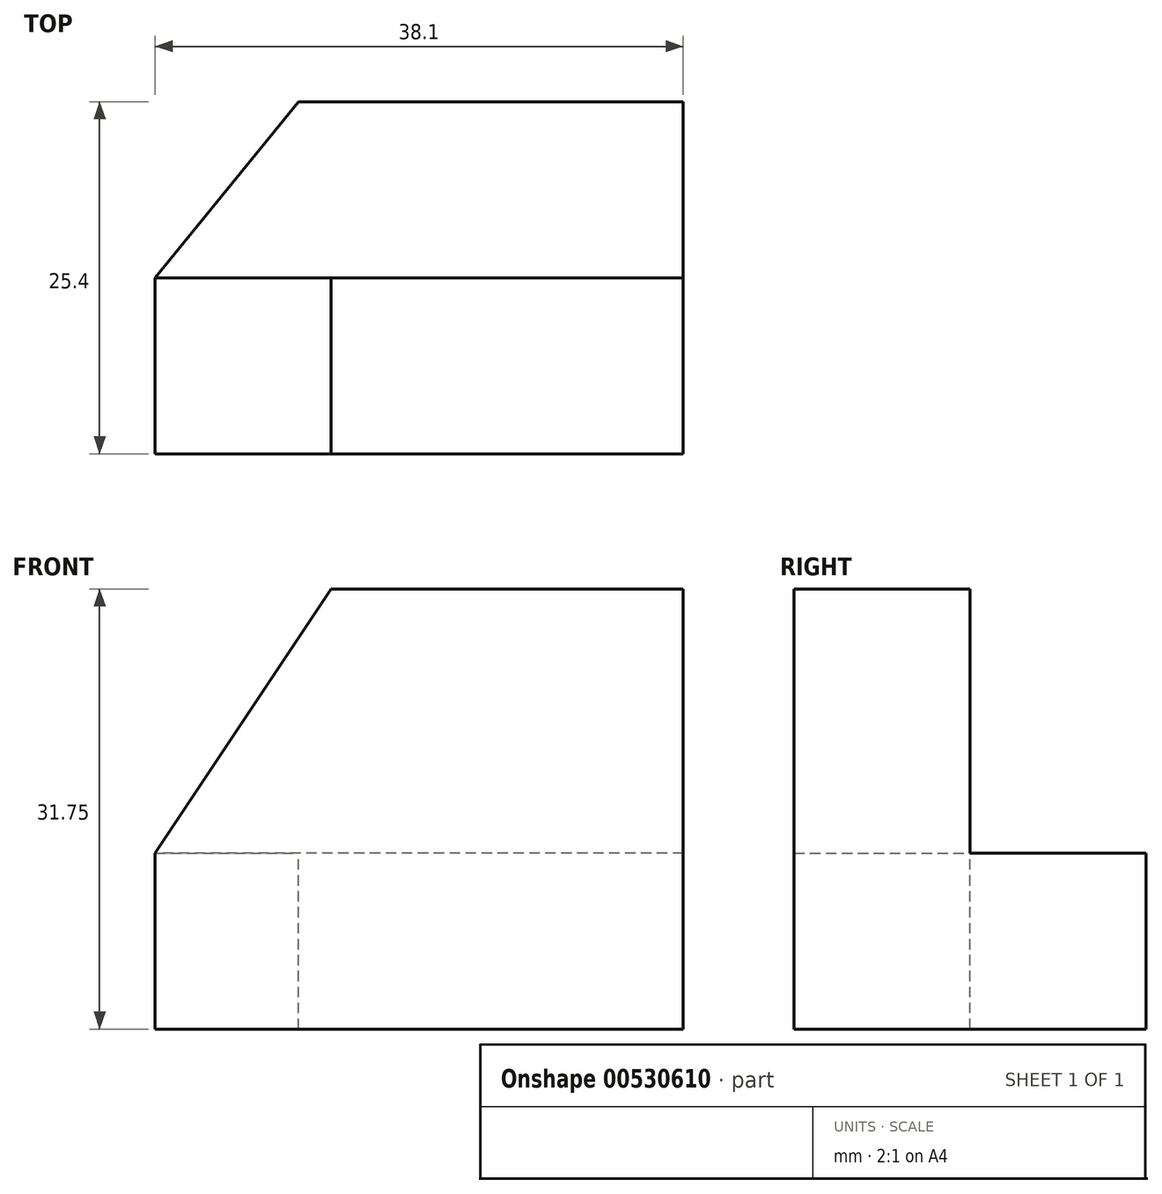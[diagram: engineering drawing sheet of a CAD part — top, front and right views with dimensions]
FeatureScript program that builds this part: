
annotation { "Feature Type Name" : "Feature", "Feature Type Description" : "" }
export const myFeature = defineFeature(function(context is Context, id is Id, definition is map)
    precondition{}
    {
        {
            var Q0;
            Q0=qCreatedBy(makeId("Right.planeOp"),FACE);
            var sketch = newSketch(context, id + "F0", { "sketchPlane" : qUnion([Q0])});
            skLineSegment(sketch, "E0", {"start": v(-25.4, 31.75) * mm, "end": v(-25.4, 0) * mm});
            skLineSegment(sketch, "E1", {"start": v(-25.4, 0) * mm, "end": v(0, 0) * mm});
            skLineSegment(sketch, "E2", {"start": v(0, 0) * mm, "end": v(0, 12.7) * mm});
            skLineSegment(sketch, "E3", {"start": v(0, 12.7) * mm, "end": v(-12.7, 12.7) * mm});
            skLineSegment(sketch, "E4", {"start": v(-12.7, 12.7) * mm, "end": v(-12.7, 31.75) * mm});
            skLineSegment(sketch, "E5", {"start": v(-12.7, 31.75) * mm, "end": v(-25.4, 31.75) * mm});
            skSolve(sketch);
        }
        {
            var Q0;
            Q0 = qSketchRegion(id + "F0", true);
            extrude(context, id + "F1", {"entities" : qUnion([Q0]), "depth" : 38.1 * mm, "offsetDistance" : 25.4 * mm});
        }
        {
            var Q0;
            Q0=makeQuery(id+"F1.opExtrude","SWEPT_FACE",FACE,{"disambiguationData":[OSD([sQuery(id+"F0.wireOp",EDGE,"E4")])]});
            var sketch = newSketch(context, id + "F2", { "sketchPlane" : qUnion([Q0])});
            skLineSegment(sketch, "E6", {"start": v(-12.7, 31.75) * mm, "end": v(0, 12.7) * mm});
            skSolve(sketch);
        }
        {
            var Q0;
            {var subQ0=sQuery(id+"F2.wireOp",EDGE,"E6");Q0=makeQuery(id+"F2.imprint","IMPRINT",FACE,{"disambiguationData":[TD([[makeQuery(id+"F2.imprint","IMPRINT",EDGE,{"derivedFrom":subQ0}),1.0]])]});}
            extrude(context, id + "F3", {"entities" : qUnion([Q0]), "operationType" : NewBodyOperationType.REMOVE, "endBound" : BoundingType.THROUGH_ALL, "oppositeDirection" : true, "depth" : 25.4 * mm, "offsetDistance" : 25.4 * mm});
        }
        {
            var Q0;
            Q0=makeQuery(id+"F1.opExtrude","SWEPT_FACE",FACE,{"disambiguationData":[OSD([sQuery(id+"F0.wireOp",EDGE,"E3")])]});
            var sketch = newSketch(context, id + "F4", { "sketchPlane" : qUnion([Q0])});
            skLineSegment(sketch, "E7", {"start": v(0, -12.7) * mm, "end": v(10.36, 0) * mm});
            skSolve(sketch);
        }
        {
            var Q0;
            {var subQ0=sQuery(id+"F4.wireOp",EDGE,"E7");Q0=makeQuery(id+"F4.imprint","IMPRINT",FACE,{"disambiguationData":[TD([[makeQuery(id+"F4.imprint","IMPRINT",EDGE,{"derivedFrom":subQ0}),1.0]])]});}
            extrude(context, id + "F5", {"entities" : qUnion([Q0]), "operationType" : NewBodyOperationType.REMOVE, "endBound" : BoundingType.THROUGH_ALL, "oppositeDirection" : true, "depth" : 25.4 * mm, "offsetDistance" : 25.4 * mm});
        }
    });
